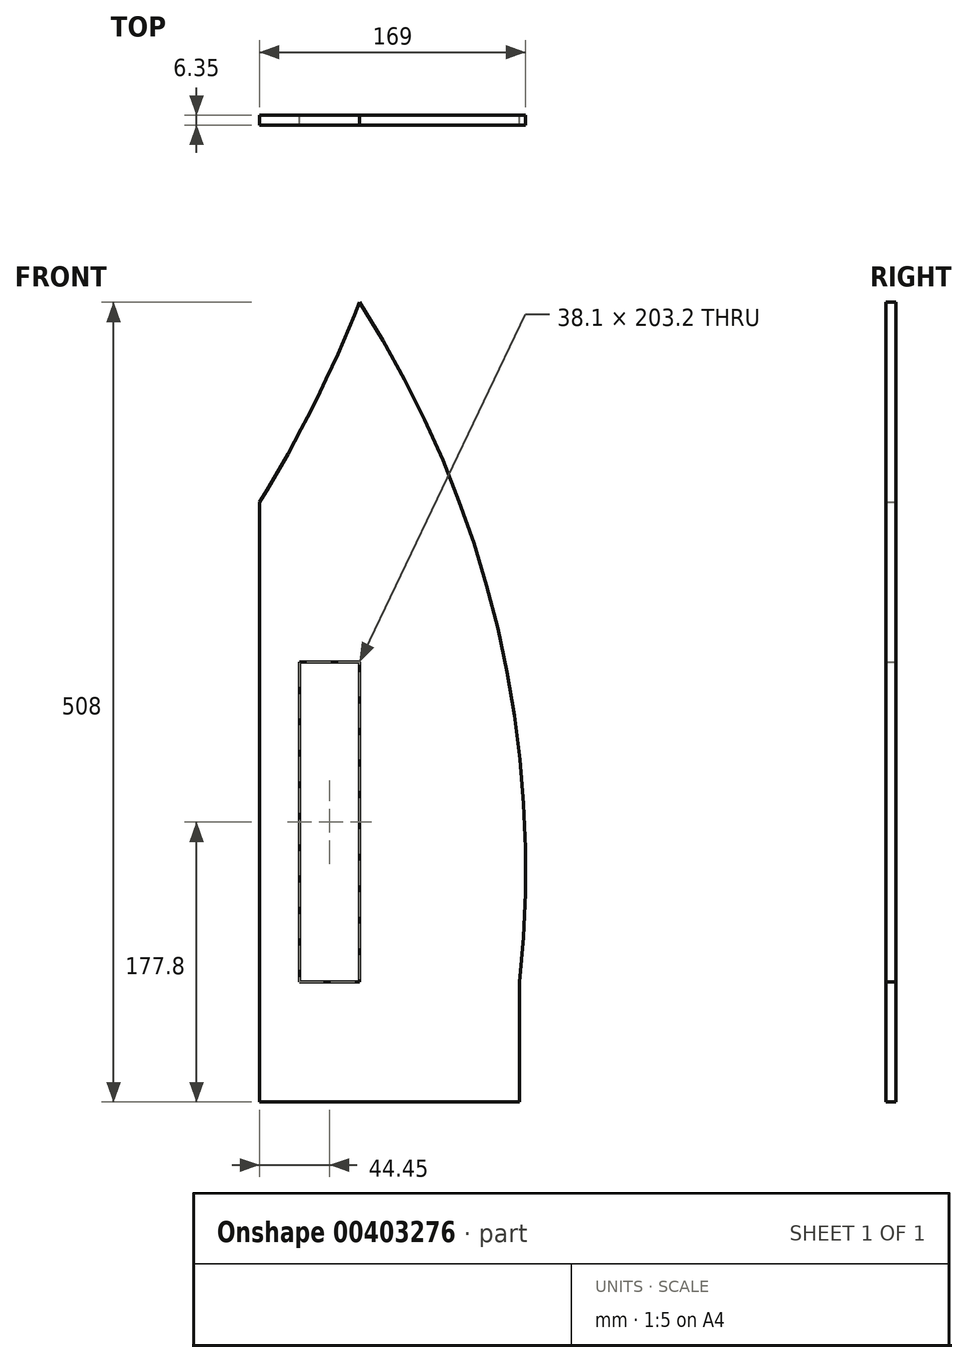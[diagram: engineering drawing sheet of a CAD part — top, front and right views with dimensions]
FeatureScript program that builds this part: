
annotation { "Feature Type Name" : "Feature", "Feature Type Description" : "" }
export const myFeature = defineFeature(function(context is Context, id is Id, definition is map)
    precondition{}
    {
        {
            var Q0;
            Q0=qCreatedBy(makeId("Front.planeOp"),FACE);
            var sketch = newSketch(context, id + "F0", { "sketchPlane" : qUnion([Q0])});
            skLineSegment(sketch, "E0", {"start": v(0, 0) * mm, "end": v(0, 304.8) * mm});
            skLineSegment(sketch, "E1.bottom", {"start": v(0, 0) * mm, "end": v(63.5, 0) * mm});
            skLineSegment(sketch, "E1.top", {"start": v(0, 431.8) * mm, "end": v(63.5, 431.8) * mm});
            skLineSegment(sketch, "E1.left", {"start": v(0, 0) * mm, "end": v(0, 431.8) * mm});
            skLineSegment(sketch, "E1.right", {"start": v(63.5, 0) * mm, "end": v(63.5, 431.8) * mm});
            skLineSegment(sketch, "E2.bottom", {"start": v(0, 0) * mm, "end": v(127, 0) * mm});
            skLineSegment(sketch, "E2.top", {"start": v(0, 304.8) * mm, "end": v(127, 304.8) * mm});
            skLineSegment(sketch, "E2.right", {"start": v(127, 0) * mm, "end": v(127, 304.8) * mm});
            skLineSegment(sketch, "E3", {"start": v(0, 0) * mm, "end": v(130.46, 0) * mm});
            skLineSegment(sketch, "E4.bottom", {"start": v(0, 0) * mm, "end": v(152.4, 0) * mm});
            skLineSegment(sketch, "E4.top", {"start": v(0, 203.2) * mm, "end": v(152.4, 203.2) * mm});
            skLineSegment(sketch, "E4.left", {"start": v(0, 0) * mm, "end": v(0, 203.2) * mm});
            skLineSegment(sketch, "E4.right", {"start": v(152.4, 0) * mm, "end": v(152.4, 203.2) * mm});
            skLineSegment(sketch, "E5", {"start": v(0, 0) * mm, "end": v(165.1, 0) * mm});
            skLineSegment(sketch, "E6.bottom", {"start": v(0, 0) * mm, "end": v(50.8, 0) * mm});
            skLineSegment(sketch, "E6.left", {"start": v(0, 0) * mm, "end": v(0, 406.4) * mm});
            skCircle(sketch, "E7", {"center": v(-497.42, 71.97) * mm, "radius": 666.41 * mm});
            skLineSegment(sketch, "E8.bottom", {"start": v(0, 0) * mm, "end": v(25.4, 0) * mm});
            skLineSegment(sketch, "E8.top", {"start": v(0, 349.25) * mm, "end": v(25.4, 349.25) * mm});
            skLineSegment(sketch, "E8.left", {"start": v(0, 0) * mm, "end": v(0, 349.25) * mm});
            skLineSegment(sketch, "E8.right", {"start": v(25.4, 0) * mm, "end": v(25.4, 349.25) * mm});
            skCircle(sketch, "E9", {"center": v(-698.5, 733.43) * mm, "radius": 819.53 * mm});
            skLineSegment(sketch, "E10.top", {"start": v(0, -76.2) * mm, "end": v(165.1, -76.2) * mm});
            skLineSegment(sketch, "E10.left", {"start": v(0, 0) * mm, "end": v(0, -76.2) * mm});
            skLineSegment(sketch, "E10.right", {"start": v(165.1, 0) * mm, "end": v(165.1, -76.2) * mm});
            skSolve(sketch);
        }
        {
            var Q0;
            {var subQ5=sQuery(id+"F0.wireOp",EDGE,"E8.bottom");Q0=makeQuery(id+"F0.imprint","IMPRINT",FACE,{"disambiguationData":[TD([[makeQuery(id+"F0.imprint","IMPRINT",EDGE,{"derivedFrom":subQ5}),1.0]])]});}
            var Q1;
            {var subQ0=sQuery(id+"F0.wireOp",EDGE,"E8.left");var subQ5=sQuery(id+"F0.wireOp",EDGE,"E4.top");var subQ6=makeQuery(id+"F0.imprint","INTERSECT",VERTEX,{"derivedFrom":[subQ5,subQ0]});Q1=makeQuery(id+"F0.imprint","IMPRINT",FACE,{"disambiguationData":[TD([[makeQuery(id+"F0.imprint","IMPRINT",EDGE,{"disambiguationData":[TD([[subQ6,-1.0]])],"derivedFrom":subQ5}),1.0]])]});}
            var Q2;
            {var subQ1=sQuery(id+"F0.wireOp",EDGE,"E2.top");var subQ3=sQuery(id+"F0.wireOp",EDGE,"E8.right");var subQ4=makeQuery(id+"F0.imprint","INTERSECT",VERTEX,{"derivedFrom":[subQ1,subQ3]});Q2=makeQuery(id+"F0.imprint","IMPRINT",FACE,{"disambiguationData":[TD([[makeQuery(id+"F0.imprint","IMPRINT",EDGE,{"disambiguationData":[TD([[subQ4,1.0]])],"derivedFrom":subQ1}),1.0]])]});}
            var Q3;
            {var subQ1=sQuery(id+"F0.wireOp",EDGE,"E1.right");var subQ3=sQuery(id+"F0.wireOp",EDGE,"E2.top");var subQ4=makeQuery(id+"F0.imprint","INTERSECT",VERTEX,{"derivedFrom":[subQ1,subQ3]});Q3=makeQuery(id+"F0.imprint","IMPRINT",FACE,{"disambiguationData":[TD([[makeQuery(id+"F0.imprint","IMPRINT",EDGE,{"disambiguationData":[TD([[subQ4,1.0]])],"derivedFrom":subQ3}),1.0]])]});}
            var Q4;
            {var subQ1=sQuery(id+"F0.wireOp",EDGE,"E1.right");var subQ3=sQuery(id+"F0.wireOp",EDGE,"E2.top");var subQ4=makeQuery(id+"F0.imprint","INTERSECT",VERTEX,{"derivedFrom":[subQ1,subQ3]});Q4=makeQuery(id+"F0.imprint","IMPRINT",FACE,{"disambiguationData":[TD([[makeQuery(id+"F0.imprint","IMPRINT",EDGE,{"disambiguationData":[TD([[subQ4,-1.0]])],"derivedFrom":subQ3}),1.0]])]});}
            var Q5;
            {var subQ0=sQuery(id+"F0.wireOp",EDGE,"E4.top");var subQ1=sQuery(id+"F0.wireOp",EDGE,"E1.right");var subQ2=makeQuery(id+"F0.imprint","INTERSECT",VERTEX,{"derivedFrom":[subQ1,subQ0]});Q5=makeQuery(id+"F0.imprint","IMPRINT",FACE,{"disambiguationData":[TD([[makeQuery(id+"F0.imprint","IMPRINT",EDGE,{"disambiguationData":[TD([[subQ2,-1.0]])],"derivedFrom":subQ1}),-1.0]])]});}
            var Q6;
            {var subQ0=sQuery(id+"F0.wireOp",EDGE,"E4.top");var subQ1=sQuery(id+"F0.wireOp",EDGE,"E1.right");var subQ2=makeQuery(id+"F0.imprint","INTERSECT",VERTEX,{"derivedFrom":[subQ1,subQ0]});Q6=makeQuery(id+"F0.imprint","IMPRINT",FACE,{"disambiguationData":[TD([[makeQuery(id+"F0.imprint","IMPRINT",EDGE,{"disambiguationData":[TD([[subQ2,-1.0]])],"derivedFrom":subQ1}),1.0]])]});}
            var Q7;
            {var subQ0=sQuery(id+"F0.wireOp",EDGE,"E6.bottom");Q7=makeQuery(id+"F0.imprint","IMPRINT",FACE,{"disambiguationData":[TD([[makeQuery(id+"F0.imprint","IMPRINT",EDGE,{"derivedFrom":subQ0}),1.0]])]});}
            var Q8;
            {var subQ0=sQuery(id+"F0.wireOp",EDGE,"E5");var subQ1=sQuery(id+"F0.wireOp",EDGE,"E1.right");var subQ2=makeQuery(id+"F0.imprint","INTERSECT",VERTEX,{"derivedFrom":[subQ1,subQ0]});Q8=makeQuery(id+"F0.imprint","IMPRINT",FACE,{"disambiguationData":[TD([[makeQuery(id+"F0.imprint","IMPRINT",EDGE,{"disambiguationData":[TD([[subQ2,-1.0]])],"derivedFrom":subQ1}),-1.0]])]});}
            var Q9;
            {var subQ4=sQuery(id+"F0.wireOp",EDGE,"E4.right");Q9=makeQuery(id+"F0.imprint","IMPRINT",FACE,{"disambiguationData":[TD([[makeQuery(id+"F0.imprint","IMPRINT",EDGE,{"derivedFrom":subQ4}),1.0]])]});}
            var Q10;
            {var subQ0=sQuery(id+"F0.wireOp",EDGE,"E4.right");Q10=makeQuery(id+"F0.imprint","IMPRINT",FACE,{"disambiguationData":[TD([[makeQuery(id+"F0.imprint","IMPRINT",EDGE,{"derivedFrom":subQ0}),-1.0]])]});}
            var Q11;
            {var subQ0=sQuery(id+"F0.wireOp",EDGE,"E8.left");var subQ1=sQuery(id+"F0.wireOp",EDGE,"E4.top");var subQ2=makeQuery(id+"F0.imprint","INTERSECT",VERTEX,{"derivedFrom":[subQ1,subQ0]});Q11=makeQuery(id+"F0.imprint","IMPRINT",FACE,{"disambiguationData":[TD([[makeQuery(id+"F0.imprint","IMPRINT",EDGE,{"disambiguationData":[TD([[subQ2,-1.0]])],"derivedFrom":subQ1}),-1.0]])]});}
            var Q12;
            {var subQ0=sQuery(id+"F0.wireOp",EDGE,"E5");var subQ3=makeQuery(id+"F0.imprint","IMPRINT",VERTEX,{"disambiguationData":[OD(0.0)],"derivedFrom":subQ0});Q12=makeQuery(id+"F0.imprint","IMPRINT",FACE,{"disambiguationData":[TD([[makeQuery(id+"F0.imprint","IMPRINT",EDGE,{"disambiguationData":[TD([[subQ3,1.0]])],"derivedFrom":subQ0}),1.0]])]});}
            var Q13;
            {var subQ0=sQuery(id+"F0.wireOp",EDGE,"E5");var subQ1=sQuery(id+"F0.wireOp",EDGE,"E1.right");var subQ2=makeQuery(id+"F0.imprint","INTERSECT",VERTEX,{"derivedFrom":[subQ1,subQ0]});Q13=makeQuery(id+"F0.imprint","IMPRINT",FACE,{"disambiguationData":[TD([[makeQuery(id+"F0.imprint","IMPRINT",EDGE,{"disambiguationData":[TD([[subQ2,-1.0]])],"derivedFrom":subQ1}),-1.0]])]});}
            var Q14;
            {var subQ3=sQuery(id+"F0.wireOp",EDGE,"E10.left");Q14=makeQuery(id+"F0.imprint","IMPRINT",FACE,{"disambiguationData":[TD([[makeQuery(id+"F0.imprint","IMPRINT",EDGE,{"derivedFrom":subQ3}),1.0]])]});}
            var Q15;
            {var subQ0=sQuery(id+"F0.wireOp",EDGE,"E10.right");Q15=makeQuery(id+"F0.imprint","IMPRINT",FACE,{"disambiguationData":[TD([[makeQuery(id+"F0.imprint","IMPRINT",EDGE,{"derivedFrom":subQ0}),-1.0]])]});}
            extrude(context, id + "F1", {"entities" : qUnion([Q0, Q1, Q2, Q3, Q4, Q5, Q6, Q7, Q8, Q9, Q10, Q11, Q12, Q13, Q14, Q15]), "depth" : 6.35 * mm});
        }
    });
